# Revit family: Gira_5022126
name_source: partatom
category: Electrical Fixtures
revit_build: Autodesk Revit 2017 (Build: 20160225_1515(x64)
units: mm (PartAtom-declared; Revit-internal decimal feet)

## family parameters
Cut with Voids When Loaded = No
Host = Face
Maintain Annotation Orientation = No
Part Type = Normal
Room Calculation Point = No
Round Connector Dimension = Use Diameter
Shared = No

## types (1)
- rocker set 2-g PB sens.4 TS4 black alum.
    BIM = https://media.live.bim.site TS4 Wippenset 2fach.rfa
    BIMSITE_PRODUCT_ID = 2f99a2c1af6ff56843ac4174688dec83021ec271
    Colour = Black
    Cost = 0 $
    Default Elevation = 1219 mm
    GTIN = 4010337072188
    HAN = 5022126
    HeinzeBIM = https://www.heinze.de
    Manufacturer = Gira
    Material = Metal
    Material quality = Aluminium
    Radio frequent bidirectional = No
    Transparent = No
    URL = https://www.gira.de

## geometry (parser evidence)
native form markers: Blend x2, Sweep x3
no freeform markers — native parametric forms only
